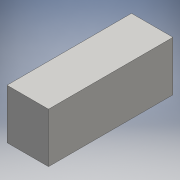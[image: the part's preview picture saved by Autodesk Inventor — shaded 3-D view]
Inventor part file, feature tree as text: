
AUTODESK INVENTOR PART (.ipt)
format: ipt  version: 2016 (Build 200138000, 138)  size: 81,920 bytes
history: native  units: mm
features: other x1, extrude x1, sketch x1
ambient origin geometry x8: Origin, YZ Plane, XZ Plane, XY Plane, X Axis, Y Axis, Z Axis, Center Point
bodies: Body1 (feature_tree)
feature tree (3):
  other  "Sólido1"
  extrude  "Extrusión1"  Depth=18.0mm
  sketch  "Boceto1"  dims[d0=45.0mm d1=18.0mm d2=15.0mm d3=0.0mm]
